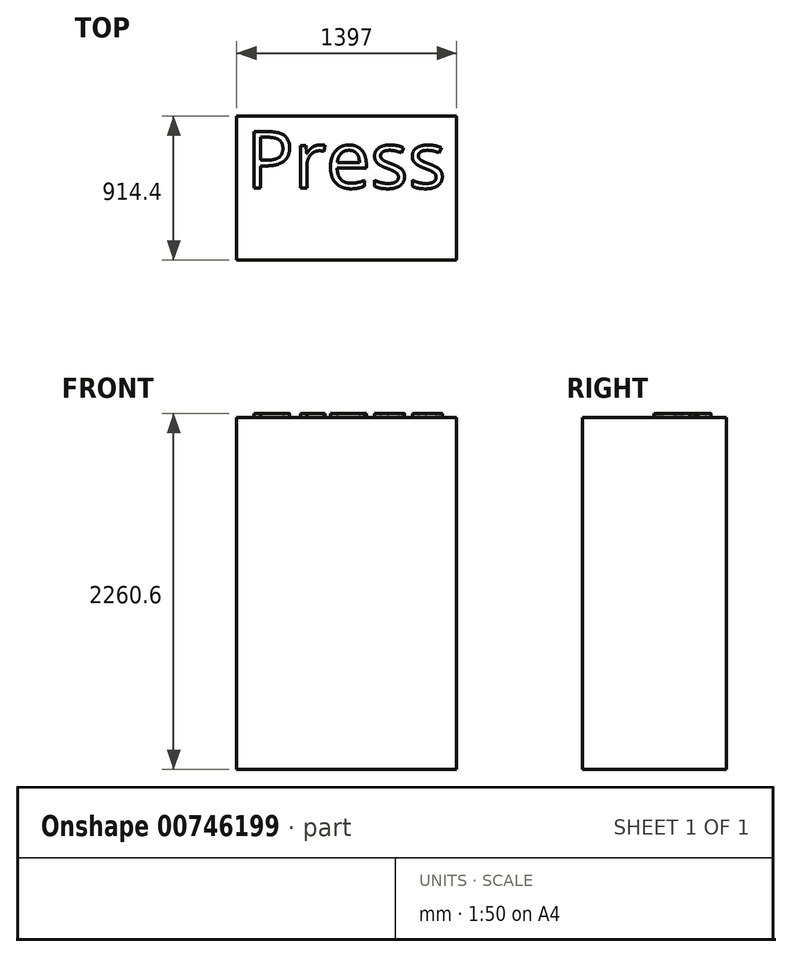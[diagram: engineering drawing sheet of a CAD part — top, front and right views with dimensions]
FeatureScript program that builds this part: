
annotation { "Feature Type Name" : "Feature", "Feature Type Description" : "" }
export const myFeature = defineFeature(function(context is Context, id is Id, definition is map)
    precondition{}
    {
        {
            var Q0;
            Q0=qCreatedBy(makeId("Top.planeOp"),FACE);
            var sketch = newSketch(context, id + "F0", { "sketchPlane" : qUnion([Q0])});
            skLineSegment(sketch, "E0.bottom", {"start": v(698.5, -457.2) * mm, "end": v(-698.5, -457.2) * mm});
            skLineSegment(sketch, "E0.top", {"start": v(698.5, 457.2) * mm, "end": v(-698.5, 457.2) * mm});
            skLineSegment(sketch, "E0.left", {"start": v(698.5, -457.2) * mm, "end": v(698.5, 457.2) * mm});
            skLineSegment(sketch, "E0.right", {"start": v(-698.5, -457.2) * mm, "end": v(-698.5, 457.2) * mm});
            skPoint(sketch, "E0.middle", {"position": v(0, 0) * mm});
            skSolve(sketch);
        }
        {
            var Q0;
            Q0 = qSketchRegion(id + "F0", true);
            extrude(context, id + "F1", {"entities" : qUnion([Q0]), "depth" : 2235.2 * mm, "offsetDistance" : 25.4 * mm});
        }
        {
            var Q0;
            Q0=makeQuery(id+"F1.opExtrude","CAP_FACE",FACE,{"disambiguationData":[OSD([sQuery(id+"F0.wireOp",EDGE,"E0.bottom"),sQuery(id+"F0.wireOp",EDGE,"E0.top"),sQuery(id+"F0.wireOp",EDGE,"E0.left"),sQuery(id+"F0.wireOp",EDGE,"E0.right")])],"isStart":false});
            var sketch = newSketch(context, id + "F2", { "sketchPlane" : qUnion([Q0])});
            skText(sketch, "E1", { "text": "Press\n", "fontName": "OpenSans-Regular.ttf"});
            const initialGuessF2  = {"E1": [-0.63954, 0, 1, 0, 0.36195]};
            skSetInitialGuess(sketch, initialGuessF2);
            skSolve(sketch);
        }
        {
            var Q0;
            Q0 = qSketchRegion(id + "F2", true);
            extrude(context, id + "F3", {"entities" : qUnion([Q0]), "operationType" : NewBodyOperationType.ADD, "depth" : 25.4 * mm, "offsetDistance" : 25.4 * mm});
        }
    });
